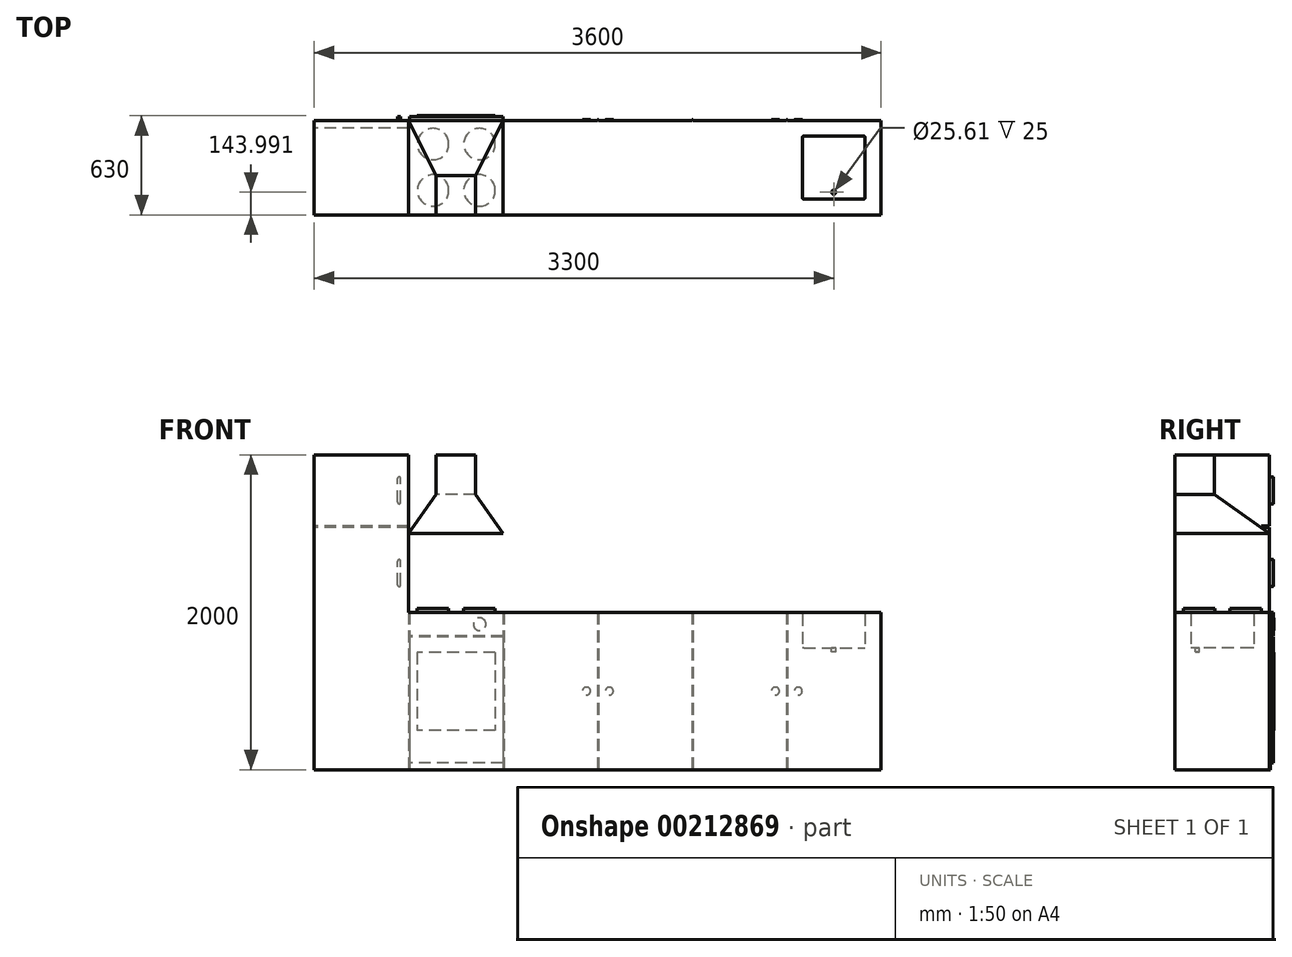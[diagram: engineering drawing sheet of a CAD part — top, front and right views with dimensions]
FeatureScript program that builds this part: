
annotation { "Feature Type Name" : "Feature", "Feature Type Description" : "" }
export const myFeature = defineFeature(function(context is Context, id is Id, definition is map)
    precondition{}
    {
        {
            var Q0;
            Q0=qCreatedBy(makeId("Top.planeOp"),FACE);
            var sketch = newSketch(context, id + "F0", { "sketchPlane" : qUnion([Q0])});
            skLineSegment(sketch, "E0.bottom", {"start": v(0, 600) * mm, "end": v(3600, 600) * mm});
            skLineSegment(sketch, "E0.top", {"start": v(0, 0) * mm, "end": v(3600, 0) * mm});
            skLineSegment(sketch, "E0.left", {"start": v(0, 600) * mm, "end": v(0, 0) * mm});
            skLineSegment(sketch, "E0.right", {"start": v(3600, 600) * mm, "end": v(3600, 0) * mm});
            skSolve(sketch);
        }
        {
            var Q0;
            Q0 = qSketchRegion(id + "F0", true);
            extrude(context, id + "F1", {"entities" : qUnion([Q0]), "depth" : 1000 * mm});
        }
        {
            var Q0;
            Q0=makeQuery(id+"F1.opExtrude","CAP_FACE",FACE,{"disambiguationData":[OSD([sQuery(id+"F0.wireOp",EDGE,"E0.bottom"),sQuery(id+"F0.wireOp",EDGE,"E0.top"),sQuery(id+"F0.wireOp",EDGE,"E0.left"),sQuery(id+"F0.wireOp",EDGE,"E0.right")])],"isStart":false});
            var sketch = newSketch(context, id + "F2", { "sketchPlane" : qUnion([Q0])});
            skLineSegment(sketch, "E1.bottom", {"start": v(3550, 550) * mm, "end": v(3050, 550) * mm});
            skLineSegment(sketch, "E1.top", {"start": v(3550, 50) * mm, "end": v(3050, 50) * mm});
            skLineSegment(sketch, "E1.left", {"start": v(3550, 550) * mm, "end": v(3550, 50) * mm});
            skLineSegment(sketch, "E1.right", {"start": v(3050, 550) * mm, "end": v(3050, 50) * mm});
            skSolve(sketch);
        }
        {
            var Q0;
            Q0 = qSketchRegion(id + "F2", true);
            extrude(context, id + "F3", {"entities" : qUnion([Q0]), "operationType" : NewBodyOperationType.REMOVE, "oppositeDirection" : true, "depth" : 250 * mm});
        }
        {
            var Q0;
            Q0=makeQuery(id+"F3.boolean.opBoolean","COPY",FACE,{"derivedFrom":makeQuery(id+"F3.opExtrude","CAP_FACE",FACE,{"disambiguationData":[OSD([sQuery(id+"F2.wireOp",EDGE,"E1.bottom"),sQuery(id+"F2.wireOp",EDGE,"E1.top"),sQuery(id+"F2.wireOp",EDGE,"E1.left"),sQuery(id+"F2.wireOp",EDGE,"E1.right")])],"isStart":false})});
            var sketch = newSketch(context, id + "F4", { "sketchPlane" : qUnion([Q0])});
            skLineSegment(sketch, "E2.bottom", {"start": v(3050, 550) * mm, "end": v(3550, 550) * mm});
            skLineSegment(sketch, "E2.top", {"start": v(3050, 50) * mm, "end": v(3550, 50) * mm});
            skLineSegment(sketch, "E2.left", {"start": v(3050, 550) * mm, "end": v(3050, 50) * mm});
            skLineSegment(sketch, "E2.right", {"start": v(3550, 550) * mm, "end": v(3550, 50) * mm});
            skSolve(sketch);
        }
        {
            var Q0;
            Q0 = qSketchRegion(id + "F4", true);
            extrude(context, id + "F5", {"entities" : qUnion([Q0]), "depth" : 25 * mm});
        }
        {
            var Q0;
            Q0=makeQuery(id+"F5.opExtrude","CAP_FACE",FACE,{"disambiguationData":[OSD([sQuery(id+"F4.wireOp",EDGE,"E2.bottom"),sQuery(id+"F4.wireOp",EDGE,"E2.top"),sQuery(id+"F4.wireOp",EDGE,"E2.left"),sQuery(id+"F4.wireOp",EDGE,"E2.right")])],"isStart":false});
            var sketch = newSketch(context, id + "F6", { "sketchPlane" : qUnion([Q0])});
            skLineSegment(sketch, "E3.bottom", {"start": v(3050, 550) * mm, "end": v(3550, 550) * mm});
            skLineSegment(sketch, "E3.top", {"start": v(3050, 50) * mm, "end": v(3550, 50) * mm});
            skLineSegment(sketch, "E3.left", {"start": v(3050, 550) * mm, "end": v(3050, 50) * mm});
            skLineSegment(sketch, "E3.right", {"start": v(3550, 550) * mm, "end": v(3550, 50) * mm});
            skLineSegment(sketch, "E4.0", {"start": v(3100, 100) * mm, "end": v(3500, 100) * mm});
            skLineSegment(sketch, "E4.1", {"start": v(3100, 500) * mm, "end": v(3100, 100) * mm});
            skLineSegment(sketch, "E4.2", {"start": v(3100, 500) * mm, "end": v(3500, 500) * mm});
            skLineSegment(sketch, "E4.3", {"start": v(3500, 500) * mm, "end": v(3500, 100) * mm});
            skSolve(sketch);
        }
        {
            var Q0;
            Q0=makeQuery(id+"F6.imprint","IMPRINT",FACE,{"disambiguationData":[TD([[makeQuery(id+"F6.imprint","IMPRINT",EDGE,{"derivedFrom":sQuery(id+"F6.wireOp",EDGE,"E3.bottom")}),1.0]])]});
            var Q1;
            Q1 = qConstructionFilter(qBodyType(qCreatedBy(id + "F6" ,EDGE), BodyType.WIRE), ConstructionObject.NO);
            var Q2;
            Q2=makeQuery(id+"F1.opExtrude","CAP_FACE",FACE,{"disambiguationData":[OSD([sQuery(id+"F0.wireOp",EDGE,"E0.bottom"),sQuery(id+"F0.wireOp",EDGE,"E0.top"),sQuery(id+"F0.wireOp",EDGE,"E0.left"),sQuery(id+"F0.wireOp",EDGE,"E0.right")])],"isStart":false});
            extrude(context, id + "F7", {"entities" : qUnion([Q0]), "operationType" : NewBodyOperationType.ADD, "surfaceEntities" : qUnion([Q1]), "endBound" : BoundingType.UP_TO_SURFACE, "endBoundEntityFace" : qUnion([Q2]), "depth" : 25 * mm});
        }
        {
            var Q0;
            Q0=makeQuery(id+"F7.opExtrude","CAP_EDGE",EDGE,{"disambiguationData":[OSD([sQuery(id+"F6.wireOp",EDGE,"E4.3")])],"isStart":false});
            var Q1;
            Q1=makeQuery(id+"F7.opExtrude","CAP_EDGE",EDGE,{"disambiguationData":[OSD([sQuery(id+"F6.wireOp",EDGE,"E4.2")])],"isStart":false});
            var Q2;
            Q2=makeQuery(id+"F7.opExtrude","CAP_EDGE",EDGE,{"disambiguationData":[OSD([sQuery(id+"F6.wireOp",EDGE,"E4.1")])],"isStart":false});
            var Q3;
            Q3=makeQuery(id+"F7.opExtrude","CAP_EDGE",EDGE,{"disambiguationData":[OSD([sQuery(id+"F6.wireOp",EDGE,"E4.0")])],"isStart":false});
            var Q4;
            Q4=makeQuery(id+"F7.opExtrude","SWEPT_EDGE",EDGE,{"disambiguationData":[OSD([sQuery(id+"F6.wireOp",EDGE,"E4.2"),sQuery(id+"F6.wireOp",EDGE,"E4.3")])]});
            var Q5;
            Q5=makeQuery(id+"F7.opExtrude","CAP_EDGE",EDGE,{"disambiguationData":[OSD([sQuery(id+"F6.wireOp",EDGE,"E4.2")])],"isStart":true});
            var Q6;
            Q6=makeQuery(id+"F7.opExtrude","CAP_EDGE",EDGE,{"disambiguationData":[OSD([sQuery(id+"F6.wireOp",EDGE,"E4.3")])],"isStart":true});
            var Q7;
            Q7=makeQuery(id+"F7.opExtrude","CAP_EDGE",EDGE,{"disambiguationData":[OSD([sQuery(id+"F6.wireOp",EDGE,"E4.0")])],"isStart":true});
            var Q8;
            Q8=makeQuery(id+"F7.opExtrude","SWEPT_EDGE",EDGE,{"disambiguationData":[OSD([sQuery(id+"F6.wireOp",EDGE,"E4.0"),sQuery(id+"F6.wireOp",EDGE,"E4.3")])]});
            var Q9;
            Q9=makeQuery(id+"F7.opExtrude","SWEPT_EDGE",EDGE,{"disambiguationData":[OSD([sQuery(id+"F6.wireOp",EDGE,"E4.0"),sQuery(id+"F6.wireOp",EDGE,"E4.1")])]});
            var Q10;
            Q10=makeQuery(id+"F7.opExtrude","CAP_EDGE",EDGE,{"disambiguationData":[OSD([sQuery(id+"F6.wireOp",EDGE,"E4.1")])],"isStart":true});
            var Q11;
            Q11=makeQuery(id+"F7.opExtrude","SWEPT_EDGE",EDGE,{"disambiguationData":[OSD([sQuery(id+"F6.wireOp",EDGE,"E4.1"),sQuery(id+"F6.wireOp",EDGE,"E4.2")])]});
            fillet(context, id + "F8", {"entities" : qUnion([Q0, Q1, Q2, Q3, Q4, Q5, Q6, Q7, Q8, Q9, Q10, Q11]), "radius" : 10 * mm, "tangentPropagation" : true, "allowEdgeOverflow" : false});
        }
        {
            var Q0;
            Q0=makeQuery(id+"F5.opExtrude","CAP_FACE",FACE,{"disambiguationData":[OSD([sQuery(id+"F4.wireOp",EDGE,"E2.bottom"),sQuery(id+"F4.wireOp",EDGE,"E2.top"),sQuery(id+"F4.wireOp",EDGE,"E2.left"),sQuery(id+"F4.wireOp",EDGE,"E2.right")])],"isStart":false});
            var sketch = newSketch(context, id + "F9", { "sketchPlane" : qUnion([Q0])});
            skCircle(sketch, "E5", {"center": v(3300, 144) * mm, "radius": 12.8 * mm});
            skLineSegment(sketch, "E6", {"start": v(3110, 144) * mm, "end": v(3490, 144) * mm, "construction": true});
            skSolve(sketch);
        }
        {
            var Q0;
            Q0 = qSketchRegion(id + "F9", true);
            extrude(context, id + "F10", {"entities" : qUnion([Q0]), "operationType" : NewBodyOperationType.REMOVE, "oppositeDirection" : true, "depth" : 25 * mm});
        }
        {
            var Q0;
            Q0=makeQuery(id+"F1.opExtrude","SWEPT_FACE",FACE,{"disambiguationData":[OSD([sQuery(id+"F0.wireOp",EDGE,"E0.bottom")])]});
            var sketch = newSketch(context, id + "F11", { "sketchPlane" : qUnion([Q0])});
            skLineSegment(sketch, "E7.bottom", {"start": v(-3005, 1000) * mm, "end": v(-3000, 1000) * mm});
            skLineSegment(sketch, "E7.top", {"start": v(-3005, 0) * mm, "end": v(-3000, 0) * mm});
            skLineSegment(sketch, "E7.left", {"start": v(-3005, 1000) * mm, "end": v(-3005, 0) * mm});
            skLineSegment(sketch, "E7.right", {"start": v(-3000, 1000) * mm, "end": v(-3000, 0) * mm});
            skLineSegment(sketch, "E8.1.0.0", {"start": v(-2400, 1000) * mm, "end": v(-2400, 0) * mm});
            skLineSegment(sketch, "E8.1.0.1", {"start": v(-2405, 1000) * mm, "end": v(-2405, 0) * mm});
            skLineSegment(sketch, "E8.1.0.2", {"start": v(-2405, 0) * mm, "end": v(-2400, 0) * mm});
            skLineSegment(sketch, "E8.1.0.3", {"start": v(-2405, 1000) * mm, "end": v(-2400, 1000) * mm});
            skLineSegment(sketch, "E8.2.0.0", {"start": v(-1800, 1000) * mm, "end": v(-1800, 0) * mm});
            skLineSegment(sketch, "E8.2.0.1", {"start": v(-1805, 1000) * mm, "end": v(-1805, 0) * mm});
            skLineSegment(sketch, "E8.2.0.2", {"start": v(-1805, 0) * mm, "end": v(-1800, 0) * mm});
            skLineSegment(sketch, "E8.2.0.3", {"start": v(-1805, 1000) * mm, "end": v(-1800, 1000) * mm});
            skLineSegment(sketch, "E8.3.0.0", {"start": v(-1200, 1000) * mm, "end": v(-1200, 0) * mm});
            skLineSegment(sketch, "E8.3.0.1", {"start": v(-1205, 1000) * mm, "end": v(-1205, 0) * mm});
            skLineSegment(sketch, "E8.3.0.2", {"start": v(-1205, 0) * mm, "end": v(-1200, 0) * mm});
            skLineSegment(sketch, "E8.3.0.3", {"start": v(-1205, 1000) * mm, "end": v(-1200, 1000) * mm});
            skLineSegment(sketch, "E8.4.0.0", {"start": v(-600, 1000) * mm, "end": v(-600, 0) * mm});
            skLineSegment(sketch, "E8.4.0.1", {"start": v(-605, 1000) * mm, "end": v(-605, 0) * mm});
            skLineSegment(sketch, "E8.4.0.2", {"start": v(-605, 0) * mm, "end": v(-600, 0) * mm});
            skLineSegment(sketch, "E8.4.0.3", {"start": v(-605, 1000) * mm, "end": v(-600, 1000) * mm});
            skLineSegment(sketch, "E8.direction1", {"start": v(-3005, 0) * mm, "end": v(-2405, 0) * mm, "construction": true});
            skCircle(sketch, "E9", {"center": v(-3075, 500) * mm, "radius": 25 * mm});
            skLineSegment(sketch, "E10", {"start": v(-3075, 1000) * mm, "end": v(-3075, 0) * mm, "construction": true});
            skLineSegment(sketch, "E11", {"start": v(-2930, 1000) * mm, "end": v(-2930, 0) * mm, "construction": true});
            skCircle(sketch, "E12", {"center": v(-2930, 500) * mm, "radius": 25 * mm});
            skCircle(sketch, "E13.1.0.0", {"center": v(-1730, 500) * mm, "radius": 25 * mm});
            skCircle(sketch, "E13.1.0.1", {"center": v(-1875, 500) * mm, "radius": 25 * mm});
            skLineSegment(sketch, "E13.direction1", {"start": v(-3075, 500) * mm, "end": v(-1875, 500) * mm, "construction": true});
            skSolve(sketch);
        }
        {
            var Q0;
            Q0 = qSketchRegion(id + "F11", true);
            extrude(context, id + "F12", {"entities" : qUnion([Q0]), "operationType" : NewBodyOperationType.ADD, "depth" : 5 * mm});
        }
        {
            var Q0;
            Q0=makeQuery(id+"F12.boolean.opBoolean","MERGE",FACE,{"derivedFrom":[makeQuery(id+"F1.opExtrude","CAP_FACE",FACE,{"disambiguationData":[OSD([sQuery(id+"F0.wireOp",EDGE,"E0.bottom"),sQuery(id+"F0.wireOp",EDGE,"E0.top"),sQuery(id+"F0.wireOp",EDGE,"E0.left"),sQuery(id+"F0.wireOp",EDGE,"E0.right")])],"isStart":false}),makeQuery(id+"F12.opExtrude","SWEPT_FACE",FACE,{"disambiguationData":[OSD([sQuery(id+"F11.wireOp",EDGE,"E7.bottom")])]}),makeQuery(id+"F12.opExtrude","SWEPT_FACE",FACE,{"disambiguationData":[OSD([sQuery(id+"F11.wireOp",EDGE,"E8.1.0.3")])]}),makeQuery(id+"F12.opExtrude","SWEPT_FACE",FACE,{"disambiguationData":[OSD([sQuery(id+"F11.wireOp",EDGE,"E8.2.0.3")])]}),makeQuery(id+"F12.opExtrude","SWEPT_FACE",FACE,{"disambiguationData":[OSD([sQuery(id+"F11.wireOp",EDGE,"E8.3.0.3")])]}),makeQuery(id+"F12.opExtrude","SWEPT_FACE",FACE,{"disambiguationData":[OSD([sQuery(id+"F11.wireOp",EDGE,"E8.4.0.3")])]})]});
            var sketch = newSketch(context, id + "F13", { "sketchPlane" : qUnion([Q0])});
            skLineSegment(sketch, "E14.bottom", {"start": v(605, 600) * mm, "end": v(1200, 600) * mm});
            skLineSegment(sketch, "E14.top", {"start": v(605, 5) * mm, "end": v(1200, 5) * mm});
            skLineSegment(sketch, "E14.left", {"start": v(605, 600) * mm, "end": v(605, 5) * mm});
            skLineSegment(sketch, "E14.right", {"start": v(1200, 600) * mm, "end": v(1200, 5) * mm});
            skCircle(sketch, "E15", {"center": v(755, 450) * mm, "radius": 100 * mm});
            skCircle(sketch, "E16.0.1.0", {"center": v(755, 155) * mm, "radius": 100 * mm});
            skCircle(sketch, "E16.1.0.0", {"center": v(1050, 450) * mm, "radius": 100 * mm});
            skCircle(sketch, "E16.1.1.0", {"center": v(1050, 155) * mm, "radius": 100 * mm});
            skLineSegment(sketch, "E16.direction1", {"start": v(755, 450) * mm, "end": v(1050, 450) * mm, "construction": true});
            skLineSegment(sketch, "E16.direction2", {"start": v(755, 450) * mm, "end": v(755, 155) * mm, "construction": true});
            skSolve(sketch);
        }
        {
            var Q0;
            Q0=makeQuery(id+"F13.imprint","IMPRINT",FACE,{"disambiguationData":[TD([[makeQuery(id+"F13.imprint","IMPRINT",EDGE,{"derivedFrom":sQuery(id+"F13.wireOp",EDGE,"E16.1.1.0")}),1.0]])]});
            var Q1;
            Q1=makeQuery(id+"F13.imprint","IMPRINT",FACE,{"disambiguationData":[TD([[makeQuery(id+"F13.imprint","IMPRINT",EDGE,{"derivedFrom":sQuery(id+"F13.wireOp",EDGE,"E16.0.1.0")}),1.0]])]});
            var Q2;
            Q2=makeQuery(id+"F13.imprint","IMPRINT",FACE,{"disambiguationData":[TD([[makeQuery(id+"F13.imprint","IMPRINT",EDGE,{"derivedFrom":sQuery(id+"F13.wireOp",EDGE,"E15")}),1.0]])]});
            var Q3;
            Q3=makeQuery(id+"F13.imprint","IMPRINT",FACE,{"disambiguationData":[TD([[makeQuery(id+"F13.imprint","IMPRINT",EDGE,{"derivedFrom":sQuery(id+"F13.wireOp",EDGE,"E16.1.0.0")}),1.0]])]});
            extrude(context, id + "F14", {"entities" : qUnion([Q0, Q1, Q2, Q3]), "depth" : 25 * mm});
        }
        {
            var Q0;
            {var subQ3=sQuery(id+"F0.wireOp",EDGE,"E0.bottom");Q0=makeQuery(id+"F12.boolean.opBoolean","SPLIT",FACE,{"disambiguationData":[TD([makeQuery(id+"F12.opExtrude","SWEPT_FACE",FACE,{"disambiguationData":[OSD([sQuery(id+"F11.wireOp",EDGE,"E8.3.0.0")])]})])],"derivedFrom":makeQuery(id+"F1.opExtrude","SWEPT_FACE",FACE,{"disambiguationData":[OSD([subQ3])]})});}
            var sketch = newSketch(context, id + "F15", { "sketchPlane" : qUnion([Q0])});
            skLineSegment(sketch, "E17.bottom", {"start": v(-1200, 1000) * mm, "end": v(-605, 1000) * mm});
            skLineSegment(sketch, "E17.top", {"start": v(-1200, 850) * mm, "end": v(-605, 850) * mm});
            skLineSegment(sketch, "E17.left", {"start": v(-1200, 1000) * mm, "end": v(-1200, 850) * mm});
            skLineSegment(sketch, "E17.right", {"start": v(-605, 1000) * mm, "end": v(-605, 850) * mm});
            skLineSegment(sketch, "E18.bottom", {"start": v(-1200, 845) * mm, "end": v(-605, 845) * mm});
            skLineSegment(sketch, "E18.top", {"start": v(-1200, 45) * mm, "end": v(-605, 45) * mm});
            skLineSegment(sketch, "E18.left", {"start": v(-1200, 845) * mm, "end": v(-1200, 45) * mm});
            skLineSegment(sketch, "E18.right", {"start": v(-605, 845) * mm, "end": v(-605, 45) * mm});
            skSolve(sketch);
        }
        {
            var Q0;
            Q0 = qSketchRegion(id + "F15", true);
            extrude(context, id + "F16", {"entities" : qUnion([Q0]), "depth" : 25 * mm});
        }
        {
            var Q0;
            Q0=makeQuery(id+"F16.opExtrude","CAP_FACE",FACE,{"disambiguationData":[OSD([sQuery(id+"F15.wireOp",EDGE,"E18.bottom"),sQuery(id+"F15.wireOp",EDGE,"E18.top"),sQuery(id+"F15.wireOp",EDGE,"E18.left"),sQuery(id+"F15.wireOp",EDGE,"E18.right")])],"isStart":false});
            var sketch = newSketch(context, id + "F17", { "sketchPlane" : qUnion([Q0])});
            skCircle(sketch, "E19", {"center": v(-1051.25, 925) * mm, "radius": 40 * mm});
            skLineSegment(sketch, "E20", {"start": v(-1200, 925) * mm, "end": v(-902.5, 925) * mm, "construction": true});
            skLineSegment(sketch, "E21", {"start": v(-902.5, 850) * mm, "end": v(-902.5, 1000) * mm, "construction": true});
            skPoint(sketch, "E21.startSnap0", {"position": v(-902.5, 845) * mm});
            skCircle(sketch, "E22.MirrorC", {"center": v(-753.75, 925) * mm, "radius": 40 * mm});
            skLineSegment(sketch, "E23.bottom", {"start": v(-1150, 745) * mm, "end": v(-655, 745) * mm});
            skLineSegment(sketch, "E23.top", {"start": v(-1150, 250) * mm, "end": v(-655, 250) * mm});
            skLineSegment(sketch, "E23.left", {"start": v(-1150, 745) * mm, "end": v(-1150, 250) * mm});
            skLineSegment(sketch, "E23.right", {"start": v(-655, 745) * mm, "end": v(-655, 250) * mm});
            skSolve(sketch);
        }
        {
            var Q0;
            Q0=makeQuery(id+"F17.imprint","IMPRINT",FACE,{"disambiguationData":[TD([[makeQuery(id+"F17.imprint","IMPRINT",EDGE,{"derivedFrom":sQuery(id+"F17.wireOp",EDGE,"E23.bottom")}),-1.0]])]});
            var Q1;
            Q1=makeQuery(id+"F17.imprint","IMPRINT",FACE,{"disambiguationData":[TD([[makeQuery(id+"F17.imprint","IMPRINT",EDGE,{"derivedFrom":sQuery(id+"F17.wireOp",EDGE,"E22.MirrorC")}),-1.0]])]});
            var Q2;
            Q2=makeQuery(id+"F17.imprint","IMPRINT",FACE,{"disambiguationData":[TD([[makeQuery(id+"F17.imprint","IMPRINT",EDGE,{"derivedFrom":sQuery(id+"F17.wireOp",EDGE,"E19")}),1.0]])]});
            extrude(context, id + "F18", {"entities" : qUnion([Q0, Q1, Q2]), "operationType" : NewBodyOperationType.ADD, "depth" : 5 * mm});
        }
        {
            var Q0;
            Q0=makeQuery(id+"F16.boolean.opBoolean","MERGE",FACE,{"derivedFrom":[makeQuery(id+"F12.boolean.opBoolean","MERGE",FACE,{"derivedFrom":[makeQuery(id+"F1.opExtrude","CAP_FACE",FACE,{"disambiguationData":[OSD([sQuery(id+"F0.wireOp",EDGE,"E0.bottom"),sQuery(id+"F0.wireOp",EDGE,"E0.top"),sQuery(id+"F0.wireOp",EDGE,"E0.left"),sQuery(id+"F0.wireOp",EDGE,"E0.right")])],"isStart":false}),makeQuery(id+"F12.opExtrude","SWEPT_FACE",FACE,{"disambiguationData":[OSD([sQuery(id+"F11.wireOp",EDGE,"E7.bottom")])]}),makeQuery(id+"F12.opExtrude","SWEPT_FACE",FACE,{"disambiguationData":[OSD([sQuery(id+"F11.wireOp",EDGE,"E8.1.0.3")])]}),makeQuery(id+"F12.opExtrude","SWEPT_FACE",FACE,{"disambiguationData":[OSD([sQuery(id+"F11.wireOp",EDGE,"E8.2.0.3")])]}),makeQuery(id+"F12.opExtrude","SWEPT_FACE",FACE,{"disambiguationData":[OSD([sQuery(id+"F11.wireOp",EDGE,"E8.3.0.3")])]}),makeQuery(id+"F12.opExtrude","SWEPT_FACE",FACE,{"disambiguationData":[OSD([sQuery(id+"F11.wireOp",EDGE,"E8.4.0.3")])]})]}),makeQuery(id+"F16.opExtrude","SWEPT_FACE",FACE,{"disambiguationData":[OSD([sQuery(id+"F15.wireOp",EDGE,"E17.bottom")])]})]});
            var sketch = newSketch(context, id + "F19", { "sketchPlane" : qUnion([Q0])});
            skLineSegment(sketch, "E24.bottom", {"start": v(0, 600) * mm, "end": v(600, 600) * mm});
            skLineSegment(sketch, "E24.top", {"start": v(0, 0) * mm, "end": v(600, 0) * mm});
            skLineSegment(sketch, "E24.left", {"start": v(0, 600) * mm, "end": v(0, 0) * mm});
            skLineSegment(sketch, "E24.right", {"start": v(600, 600) * mm, "end": v(600, 0) * mm});
            skSolve(sketch);
        }
        {
            var Q0;
            Q0 = qSketchRegion(id + "F19", true);
            extrude(context, id + "F20", {"entities" : qUnion([Q0]), "operationType" : NewBodyOperationType.ADD, "depth" : 1000 * mm});
        }
        {
            var Q0;
            {var subQ1=sQuery(id+"F0.wireOp",EDGE,"E0.left");var subQ3=sQuery(id+"F0.wireOp",EDGE,"E0.bottom");Q0=makeQuery(id+"F20.boolean.opBoolean","MERGE",FACE,{"derivedFrom":[makeQuery(id+"F12.boolean.opBoolean","SPLIT",FACE,{"disambiguationData":[TD([makeQuery(id+"F1.opExtrude","SWEPT_FACE",FACE,{"disambiguationData":[OSD([subQ1])]})])],"derivedFrom":makeQuery(id+"F1.opExtrude","SWEPT_FACE",FACE,{"disambiguationData":[OSD([subQ3])]})}),makeQuery(id+"F20.opExtrude","SWEPT_FACE",FACE,{"disambiguationData":[OSD([sQuery(id+"F19.wireOp",EDGE,"E24.bottom")])]})]});}
            var sketch = newSketch(context, id + "F21", { "sketchPlane" : qUnion([Q0])});
            skLineSegment(sketch, "E25.bottom", {"start": v(-600, 1550) * mm, "end": v(0, 1550) * mm});
            skLineSegment(sketch, "E25.top", {"start": v(-600, 1540) * mm, "end": v(0, 1540) * mm});
            skLineSegment(sketch, "E25.left", {"start": v(-600, 1550) * mm, "end": v(-600, 1540) * mm});
            skLineSegment(sketch, "E25.right", {"start": v(0, 1550) * mm, "end": v(0, 1540) * mm});
            skSolve(sketch);
        }
        {
            var Q0;
            Q0 = qSketchRegion(id + "F21", true);
            extrude(context, id + "F22", {"entities" : qUnion([Q0]), "operationType" : NewBodyOperationType.REMOVE, "oppositeDirection" : true, "depth" : 50 * mm});
        }
        {
            var Q0;
            {var subQ1=sQuery(id+"F0.wireOp",EDGE,"E0.left");var subQ2=makeQuery(id+"F1.opExtrude","SWEPT_FACE",FACE,{"disambiguationData":[OSD([subQ1])]});var subQ4=sQuery(id+"F19.wireOp",EDGE,"E24.bottom");var subQ7=sQuery(id+"F0.wireOp",EDGE,"E0.bottom");Q0=makeQuery(id+"F22.boolean.opBoolean","SPLIT",FACE,{"disambiguationData":[TD([makeQuery(id+"F22.opExtrude","SWEPT_FACE",FACE,{"disambiguationData":[OSD([sQuery(id+"F21.wireOp",EDGE,"E25.bottom")])]})])],"derivedFrom":makeQuery(id+"F20.boolean.opBoolean","MERGE",FACE,{"derivedFrom":[makeQuery(id+"F12.boolean.opBoolean","SPLIT",FACE,{"disambiguationData":[TD([subQ2])],"derivedFrom":makeQuery(id+"F1.opExtrude","SWEPT_FACE",FACE,{"disambiguationData":[OSD([subQ7])]})}),makeQuery(id+"F20.opExtrude","SWEPT_FACE",FACE,{"disambiguationData":[OSD([subQ4])]})]})});}
            var sketch = newSketch(context, id + "F23", { "sketchPlane" : qUnion([Q0])});
            skLineSegment(sketch, "E26", {"start": v(-600, 1775) * mm, "end": v(0, 1775) * mm, "construction": true});
            skLineSegment(sketch, "E27", {"start": v(-550, 1775) * mm, "end": v(-550, 1850) * mm});
            skLineSegment(sketch, "E28", {"start": v(-530, 1775) * mm, "end": v(-530, 1850) * mm});
            skArc(sketch, "E29", {"start": v(-550, 1850) * mm, "mid": v(-540, 1860) * mm, "end": v(-530, 1850) * mm});
            skLineSegment(sketch, "E30.MirrorCS", {"start": v(-530, 1775) * mm, "end": v(-530, 1700) * mm});
            skLineSegment(sketch, "E31.MirrorCS", {"start": v(-550, 1775) * mm, "end": v(-550, 1700) * mm});
            skArc(sketch, "E32.MirrorCS", {"start": v(-550, 1700) * mm, "mid": v(-540, 1690) * mm, "end": v(-530, 1700) * mm});
            skLineSegment(sketch, "E33", {"start": v(-550, 1249.89) * mm, "end": v(-550, 1324.89) * mm});
            skLineSegment(sketch, "E34", {"start": v(-530, 1249.89) * mm, "end": v(-530, 1324.89) * mm});
            skArc(sketch, "E35", {"start": v(-550, 1324.89) * mm, "mid": v(-540, 1334.89) * mm, "end": v(-530, 1324.89) * mm});
            skLineSegment(sketch, "E36.MirrorCS", {"start": v(-530, 1249.89) * mm, "end": v(-530, 1174.89) * mm});
            skLineSegment(sketch, "E37.MirrorCS", {"start": v(-550, 1249.89) * mm, "end": v(-550, 1174.89) * mm});
            skArc(sketch, "E38.MirrorCS", {"start": v(-550, 1174.89) * mm, "mid": v(-540, 1164.89) * mm, "end": v(-530, 1174.89) * mm});
            skSolve(sketch);
        }
        {
            var Q0;
            Q0 = qSketchRegion(id + "F23", true);
            extrude(context, id + "F24", {"entities" : qUnion([Q0]), "operationType" : NewBodyOperationType.ADD, "depth" : 25 * mm});
        }
        {
            var Q0;
            Q0=makeQuery(id+"F20.opExtrude","CAP_FACE",FACE,{"disambiguationData":[OSD([sQuery(id+"F19.wireOp",EDGE,"E24.bottom"),sQuery(id+"F19.wireOp",EDGE,"E24.top"),sQuery(id+"F19.wireOp",EDGE,"E24.left"),sQuery(id+"F19.wireOp",EDGE,"E24.right")])],"isStart":false});
            var sketch = newSketch(context, id + "F25", { "sketchPlane" : qUnion([Q0])});
            skLineSegment(sketch, "E39.bottom", {"start": v(1025, 250) * mm, "end": v(775, 250) * mm});
            skLineSegment(sketch, "E39.top", {"start": v(1025, 0) * mm, "end": v(775, 0) * mm});
            skLineSegment(sketch, "E39.left", {"start": v(1025, 250) * mm, "end": v(1025, 0) * mm});
            skLineSegment(sketch, "E39.right", {"start": v(775, 250) * mm, "end": v(775, 0) * mm});
            skSolve(sketch);
        }
        {
            var Q0;
            Q0 = qSketchRegion(id + "F25", true);
            extrude(context, id + "F26", {"entities" : qUnion([Q0]), "oppositeDirection" : true, "depth" : 250 * mm});
        }
        {
            var Q0;
            Q0=makeQuery(id+"F26.opExtrude","CAP_FACE",FACE,{"disambiguationData":[OSD([sQuery(id+"F25.wireOp",EDGE,"E39.bottom"),sQuery(id+"F25.wireOp",EDGE,"E39.top"),sQuery(id+"F25.wireOp",EDGE,"E39.left"),sQuery(id+"F25.wireOp",EDGE,"E39.right")])],"isStart":false});
            cPlane(context, id + "F27", {"entities" : qUnion([Q0]), "cplaneType" : CPlaneType.OFFSET, "offset" : 250 * mm, "width" : 150 * mm, "height" : 150 * mm});
        }
        {
            var Q0;
            Q0=qCreatedBy(id+"F27.planeOp",FACE);
            var sketch = newSketch(context, id + "F28", { "sketchPlane" : qUnion([Q0])});
            skLineSegment(sketch, "E40.bottom", {"start": v(600, 0) * mm, "end": v(1200, 0) * mm});
            skLineSegment(sketch, "E40.top", {"start": v(600, -600) * mm, "end": v(1200, -600) * mm});
            skLineSegment(sketch, "E40.left", {"start": v(600, 0) * mm, "end": v(600, -600) * mm});
            skLineSegment(sketch, "E40.right", {"start": v(1200, 0) * mm, "end": v(1200, -600) * mm});
            skSolve(sketch);
        }
        {
            var Q1;
            Q1=makeQuery(id+"F26.opExtrude","CAP_FACE",FACE,{"disambiguationData":[OSD([sQuery(id+"F25.wireOp",EDGE,"E39.bottom"),sQuery(id+"F25.wireOp",EDGE,"E39.top"),sQuery(id+"F25.wireOp",EDGE,"E39.left"),sQuery(id+"F25.wireOp",EDGE,"E39.right")])],"isStart":false});
            var Q2;
            Q2=makeQuery(id+"F28.imprint","IMPRINT",FACE,{"disambiguationData":[TD([[makeQuery(id+"F28.imprint","IMPRINT",EDGE,{"derivedFrom":sQuery(id+"F28.wireOp",EDGE,"E40.bottom")}),-1.0]])]});
            loft(context, id + "F29", {"operationType" : NewBodyOperationType.ADD, "sheetProfilesArray" : [{ "sheetProfileEntities" : qUnion([Q1]) }, { "sheetProfileEntities" : qUnion([Q2]) }]});
        }
    });
